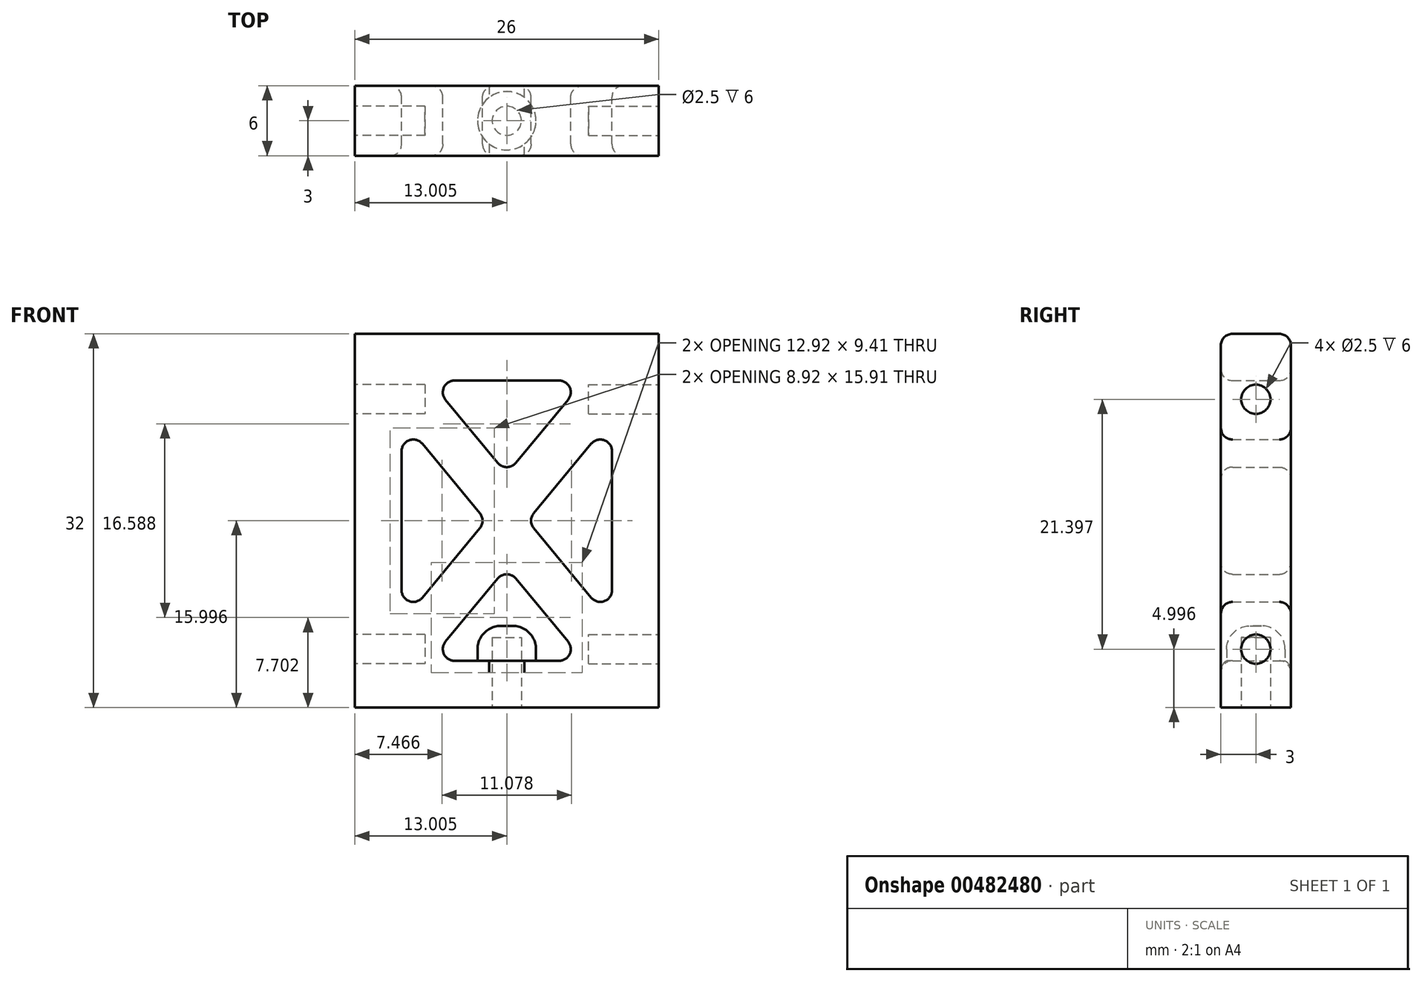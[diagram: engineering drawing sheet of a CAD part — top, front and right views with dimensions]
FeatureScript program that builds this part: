
annotation { "Feature Type Name" : "Feature", "Feature Type Description" : "" }
export const myFeature = defineFeature(function(context is Context, id is Id, definition is map)
    precondition{}
    {
        {
            var Q0;
            Q0=qCreatedBy(makeId("Front.planeOp"),FACE);
            var sketch = newSketch(context, id + "F0", { "sketchPlane" : qUnion([Q0])});
            skLineSegment(sketch, "E0.bottom", {"start": v(-3.25, 17.43) * mm, "end": v(-29.25, 17.43) * mm});
            skLineSegment(sketch, "E0.top", {"start": v(-3.25, 49.43) * mm, "end": v(-29.25, 49.43) * mm});
            skLineSegment(sketch, "E0.left", {"start": v(-3.25, 17.43) * mm, "end": v(-3.25, 49.43) * mm});
            skLineSegment(sketch, "E0.right", {"start": v(-29.25, 17.43) * mm, "end": v(-29.25, 49.43) * mm});
            skPoint(sketch, "E0.middle", {"position": v(-16.25, 33.43) * mm});
            skLineSegment(sketch, "E1.0", {"start": v(-11.77, 45.43) * mm, "end": v(-20.72, 45.43) * mm});
            skLineSegment(sketch, "E1.1", {"start": v(-7.25, 27.47) * mm, "end": v(-7.25, 39.38) * mm});
            skLineSegment(sketch, "E1.2", {"start": v(-11.77, 21.43) * mm, "end": v(-20.72, 21.43) * mm});
            skLineSegment(sketch, "E1.3", {"start": v(-25.25, 27.47) * mm, "end": v(-25.25, 39.38) * mm});
            skLineSegment(sketch, "E2", {"start": v(-23.47, 40.02) * mm, "end": v(-18.55, 34.06) * mm});
            skLineSegment(sketch, "E3.MirrorCS", {"start": v(-23.47, 26.83) * mm, "end": v(-18.55, 32.79) * mm});
            skLineSegment(sketch, "E4.MirrorCS", {"start": v(-9.02, 40.02) * mm, "end": v(-13.94, 34.06) * mm});
            skLineSegment(sketch, "E5.MirrorCS", {"start": v(-9.02, 26.83) * mm, "end": v(-13.94, 32.79) * mm});
            skLineSegment(sketch, "E6", {"start": v(-21.49, 43.79) * mm, "end": v(-17.02, 38.38) * mm});
            skLineSegment(sketch, "E7.MirrorCS", {"start": v(-21.49, 23.06) * mm, "end": v(-17.02, 28.48) * mm});
            skLineSegment(sketch, "E8.MirrorCS", {"start": v(-11, 43.79) * mm, "end": v(-15.47, 38.38) * mm});
            skLineSegment(sketch, "E9.MirrorCS", {"start": v(-11, 23.06) * mm, "end": v(-15.47, 28.48) * mm});
            skPoint(sketch, "E10.visualSharp", {"position": v(-25.25, 24.7) * mm});
            skArc(sketch, "E10.filletArc", {"start": v(-25.25, 27.47) * mm, "mid": v(-24.58, 26.53) * mm, "end": v(-23.47, 26.83) * mm});
            skPoint(sketch, "E11.visualSharp", {"position": v(-7.25, 24.7) * mm});
            skArc(sketch, "E11.filletArc", {"start": v(-9.02, 26.83) * mm, "mid": v(-7.9, 26.53) * mm, "end": v(-7.25, 27.47) * mm});
            skPoint(sketch, "E12.visualSharp", {"position": v(-7.25, 42.16) * mm});
            skArc(sketch, "E12.filletArc", {"start": v(-7.25, 39.38) * mm, "mid": v(-7.9, 40.32) * mm, "end": v(-9.02, 40.02) * mm});
            skPoint(sketch, "E13.visualSharp", {"position": v(-25.25, 42.16) * mm});
            skArc(sketch, "E13.filletArc", {"start": v(-23.47, 40.02) * mm, "mid": v(-24.58, 40.32) * mm, "end": v(-25.25, 39.38) * mm});
            skPoint(sketch, "E14.visualSharp", {"position": v(-22.84, 45.43) * mm});
            skArc(sketch, "E14.filletArc", {"start": v(-20.72, 45.43) * mm, "mid": v(-21.62, 44.85) * mm, "end": v(-21.49, 43.79) * mm});
            skPoint(sketch, "E15.visualSharp", {"position": v(-9.65, 45.43) * mm});
            skArc(sketch, "E15.filletArc", {"start": v(-11, 43.79) * mm, "mid": v(-10.87, 44.85) * mm, "end": v(-11.77, 45.43) * mm});
            skPoint(sketch, "E16.visualSharp", {"position": v(-9.65, 21.43) * mm});
            skArc(sketch, "E16.filletArc", {"start": v(-11.77, 21.43) * mm, "mid": v(-10.87, 22) * mm, "end": v(-11, 23.06) * mm});
            skPoint(sketch, "E17.visualSharp", {"position": v(-22.84, 21.43) * mm});
            skArc(sketch, "E17.filletArc", {"start": v(-21.49, 23.06) * mm, "mid": v(-21.62, 22) * mm, "end": v(-20.72, 21.43) * mm});
            skPoint(sketch, "E18.visualSharp", {"position": v(-14.46, 33.43) * mm});
            skArc(sketch, "E18.filletArc", {"start": v(-13.94, 34.06) * mm, "mid": v(-14.17, 33.43) * mm, "end": v(-13.94, 32.79) * mm});
            skPoint(sketch, "E19.visualSharp", {"position": v(-16.25, 37.44) * mm});
            skArc(sketch, "E19.filletArc", {"start": v(-17.02, 38.38) * mm, "mid": v(-16.25, 38.01) * mm, "end": v(-15.47, 38.38) * mm});
            skPoint(sketch, "E20.visualSharp", {"position": v(-18.03, 33.43) * mm});
            skArc(sketch, "E20.filletArc", {"start": v(-18.55, 32.79) * mm, "mid": v(-18.32, 33.43) * mm, "end": v(-18.55, 34.06) * mm});
            skPoint(sketch, "E21.visualSharp", {"position": v(-16.25, 29.4) * mm});
            skArc(sketch, "E21.filletArc", {"start": v(-15.47, 28.48) * mm, "mid": v(-16.25, 28.84) * mm, "end": v(-17.02, 28.48) * mm});
            skSolve(sketch);
        }
        {
            var Q0;
            Q0 = qSketchRegion(id + "F0", true);
            extrude(context, id + "F1", {"entities" : qUnion([Q0]), "depth" : 6 * mm, "offsetDistance" : 25 * mm});
        }
        {
            var Q0;
            Q0=makeQuery(id+"F1.opExtrude","SWEPT_FACE",FACE,{"disambiguationData":[OSD([sQuery(id+"F0.wireOp",EDGE,"E0.left")])]});
            var sketch = newSketch(context, id + "F2", { "sketchPlane" : qUnion([Q0])});
            skLineSegment(sketch, "E22", {"start": v(-3, 49.43) * mm, "end": v(-3, 17.43) * mm, "construction": true});
            skCircle(sketch, "E23", {"center": v(-3, 22.43) * mm, "radius": 1.25 * mm});
            skCircle(sketch, "E24", {"center": v(-3, 43.82) * mm, "radius": 1.25 * mm});
            skSolve(sketch);
        }
        {
            var Q0;
            Q0=makeQuery(id+"F1.opExtrude","SWEPT_FACE",FACE,{"disambiguationData":[OSD([sQuery(id+"F0.wireOp",EDGE,"E0.right")])]});
            var sketch = newSketch(context, id + "F3", { "sketchPlane" : qUnion([Q0])});
            skLineSegment(sketch, "E25", {"start": v(3, 49.43) * mm, "end": v(3, 17.43) * mm, "construction": true});
            skCircle(sketch, "E26", {"center": v(3, 22.43) * mm, "radius": 1.25 * mm});
            skCircle(sketch, "E27", {"center": v(3, 43.82) * mm, "radius": 1.25 * mm});
            skSolve(sketch);
        }
        {
            var Q0;
            Q0 = qSketchRegion(id + "F3", true);
            extrude(context, id + "F4", {"entities" : qUnion([Q0]), "operationType" : NewBodyOperationType.REMOVE, "oppositeDirection" : true, "depth" : 6 * mm, "offsetDistance" : 25 * mm});
        }
        {
            var Q0;
            Q0 = qSketchRegion(id + "F2", true);
            extrude(context, id + "F5", {"entities" : qUnion([Q0]), "operationType" : NewBodyOperationType.REMOVE, "oppositeDirection" : true, "depth" : 6 * mm, "offsetDistance" : 25 * mm});
        }
        {
            var Q0;
            Q0=makeQuery(id+"F1.opExtrude","SWEPT_FACE",FACE,{"disambiguationData":[OSD([sQuery(id+"F0.wireOp",EDGE,"E1.2")])]});
            var sketch = newSketch(context, id + "F6", { "sketchPlane" : qUnion([Q0])});
            skLineSegment(sketch, "E28", {"start": v(-28.08, -3) * mm, "end": v(-4.4, -3) * mm, "construction": true});
            skCircle(sketch, "E29", {"center": v(-16.25, -3) * mm, "radius": 2.5 * mm});
            skSolve(sketch);
        }
        {
            var Q0;
            Q0 = qSketchRegion(id + "F6", true);
            extrude(context, id + "F7", {"entities" : qUnion([Q0]), "operationType" : NewBodyOperationType.ADD, "depth" : 3 * mm, "offsetDistance" : 25 * mm});
        }
        {
            var Q0;
            Q0=makeQuery(id+"F1.opExtrude","SWEPT_FACE",FACE,{"disambiguationData":[OSD([sQuery(id+"F0.wireOp",EDGE,"E0.bottom")])]});
            var sketch = newSketch(context, id + "F8", { "sketchPlane" : qUnion([Q0])});
            skCircle(sketch, "E30", {"center": v(-16.25, 3) * mm, "radius": 1.25 * mm});
            skSolve(sketch);
        }
        {
            var Q0;
            Q0=makeQuery(id+"F8.imprint","IMPRINT",FACE,{"disambiguationData":[TD([[makeQuery(id+"F8.imprint","IMPRINT",EDGE,{"derivedFrom":sQuery(id+"F8.wireOp",EDGE,"E30")}),1.0]])]});
            extrude(context, id + "F9", {"entities" : qUnion([Q0]), "operationType" : NewBodyOperationType.REMOVE, "oppositeDirection" : true, "depth" : 6 * mm, "offsetDistance" : 25 * mm});
        }
        {
            var Q0;
            Q0=makeQuery(id+"F1.opExtrude","CAP_EDGE",EDGE,{"disambiguationData":[OSD([sQuery(id+"F0.wireOp",EDGE,"E4.MirrorCS")])],"isStart":true});
            var Q1;
            Q1=makeQuery(id+"F1.opExtrude","CAP_EDGE",EDGE,{"disambiguationData":[OSD([sQuery(id+"F0.wireOp",EDGE,"E8.MirrorCS")])],"isStart":true});
            var Q2;
            Q2=makeQuery(id+"F1.opExtrude","CAP_EDGE",EDGE,{"disambiguationData":[OSD([sQuery(id+"F0.wireOp",EDGE,"E2")])],"isStart":true});
            var Q3;
            Q3=makeQuery(id+"F1.opExtrude","CAP_EDGE",EDGE,{"disambiguationData":[OSD([sQuery(id+"F0.wireOp",EDGE,"E7.MirrorCS")])],"isStart":true});
            var Q4;
            Q4=makeQuery(id+"F1.opExtrude","CAP_EDGE",EDGE,{"disambiguationData":[OSD([sQuery(id+"F0.wireOp",EDGE,"E6")])],"isStart":false});
            var Q5;
            Q5=makeQuery(id+"F1.opExtrude","CAP_EDGE",EDGE,{"disambiguationData":[OSD([sQuery(id+"F0.wireOp",EDGE,"E1.3")])],"isStart":false});
            var Q6;
            Q6=makeQuery(id+"F1.opExtrude","CAP_EDGE",EDGE,{"disambiguationData":[OSD([sQuery(id+"F0.wireOp",EDGE,"E5.MirrorCS")])],"isStart":false});
            var Q7;
            Q7=makeQuery(id+"F1.opExtrude","CAP_EDGE",EDGE,{"disambiguationData":[OSD([sQuery(id+"F0.wireOp",EDGE,"E9.MirrorCS")])],"isStart":false});
            fillet(context, id + "F10", {"entities" : qUnion([Q0, Q1, Q2, Q3, Q4, Q5, Q6, Q7]), "radius" : 1 * mm, "tangentPropagation" : true, "allowEdgeOverflow" : false});
        }
        {
            var Q0;
            Q0=makeQuery(id+"F1.opExtrude","CAP_EDGE",EDGE,{"disambiguationData":[OSD([sQuery(id+"F0.wireOp",EDGE,"E0.top")])],"isStart":true});
            var Q1;
            Q1=makeQuery(id+"F1.opExtrude","CAP_EDGE",EDGE,{"disambiguationData":[OSD([sQuery(id+"F0.wireOp",EDGE,"E0.top")])],"isStart":false});
            fillet(context, id + "F11", {"entities" : qUnion([Q0, Q1]), "radius" : 1 * mm, "tangentPropagation" : true, "allowEdgeOverflow" : false});
        }
        {
            var Q0;
            Q0=makeQuery(id+"F7.opExtrude","CAP_EDGE",EDGE,{"disambiguationData":[OSD([sQuery(id+"F6.wireOp",EDGE,"E29")])],"isStart":false});
            fillet(context, id + "F12", {"entities" : qUnion([Q0]), "radius" : 2 * mm, "tangentPropagation" : true, "allowEdgeOverflow" : false});
        }
    });
